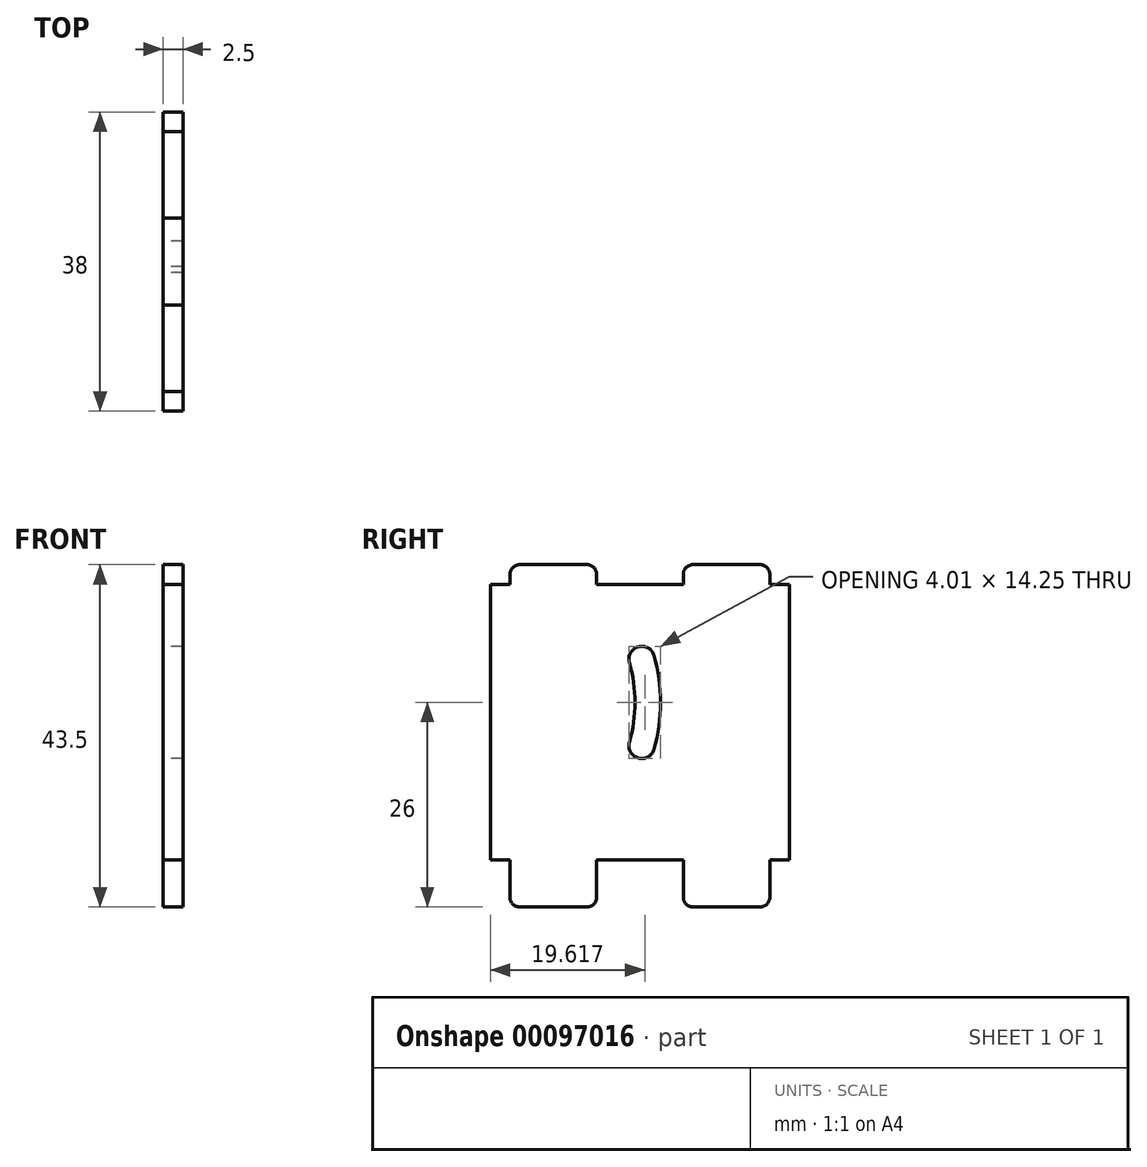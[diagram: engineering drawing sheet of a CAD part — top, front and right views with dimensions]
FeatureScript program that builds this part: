
annotation { "Feature Type Name" : "Feature", "Feature Type Description" : "" }
export const myFeature = defineFeature(function(context is Context, id is Id, definition is map)
    precondition{}
    {
        {
            var Q0;
            Q0=qCreatedBy(makeId("Right.planeOp"),FACE);
            var sketch = newSketch(context, id + "F0", { "sketchPlane" : qUnion([Q0])});
            skLineSegment(sketch, "E0.bottom", {"start": v(-19, 17.5) * mm, "end": v(-16.5, 17.5) * mm});
            skLineSegment(sketch, "E0.top", {"start": v(-19, -17.5) * mm, "end": v(-16.5, -17.5) * mm});
            skLineSegment(sketch, "E0.left", {"start": v(-19, 17.5) * mm, "end": v(-19, -17.5) * mm});
            skLineSegment(sketch, "E0.right", {"start": v(19, 17.5) * mm, "end": v(19, -17.5) * mm});
            skPoint(sketch, "E0.middle", {"position": v(0, 0) * mm});
            skPoint(sketch, "E1", {"position": v(-19, 2.5) * mm});
            skLineSegment(sketch, "E2", {"start": v(-19, 2.5) * mm, "end": v(-0.63, 2.82) * mm});
            skLineSegment(sketch, "E3", {"start": v(-19, 2.5) * mm, "end": v(-1.34, -2.56) * mm});
            skLineSegment(sketch, "E4", {"start": v(-19, 2.5) * mm, "end": v(-1.34, 7.56) * mm});
            skArc(sketch, "E5", {"start": v(1.79, 8.46) * mm, "mid": v(-0.22, 9.57) * mm, "end": v(-1.34, 7.56) * mm});
            skArc(sketch, "E6", {"start": v(-1.34, -2.56) * mm, "mid": v(-0.22, -4.57) * mm, "end": v(1.79, -3.46) * mm});
            skPoint(sketch, "E7", {"position": v(-0.63, 2.82) * mm});
            skPoint(sketch, "E8", {"position": v(-1.34, 7.56) * mm});
            skPoint(sketch, "E9", {"position": v(-1.34, -2.56) * mm});
            skArc(sketch, "E10", {"start": v(1.79, -3.46) * mm, "mid": v(2.62, 2.5) * mm, "end": v(1.79, 8.46) * mm});
            skArc(sketch, "E11", {"start": v(-1.34, -2.56) * mm, "mid": v(-0.63, 2.5) * mm, "end": v(-1.34, 7.56) * mm});
            skPoint(sketch, "E12.end.orphan", {"position": v(2.62, 2.82) * mm});
            skLineSegment(sketch, "E13.bottom", {"start": v(-5.5, 17.5) * mm, "end": v(5.5, 17.5) * mm});
            skLineSegment(sketch, "E13.top", {"start": v(-15.25, 20) * mm, "end": v(-6.75, 20) * mm});
            skLineSegment(sketch, "E13.left", {"start": v(-16.5, 17.5) * mm, "end": v(-16.5, 18.75) * mm});
            skLineSegment(sketch, "E13.right", {"start": v(16.5, 17.5) * mm, "end": v(16.5, 18.75) * mm});
            skLineSegment(sketch, "E14.bottom", {"start": v(-5.5, -17.5) * mm, "end": v(5.5, -17.5) * mm});
            skLineSegment(sketch, "E14.top", {"start": v(-15.25, -23.5) * mm, "end": v(-6.75, -23.5) * mm});
            skLineSegment(sketch, "E14.left", {"start": v(-16.5, -17.5) * mm, "end": v(-16.5, -22.25) * mm});
            skLineSegment(sketch, "E14.right", {"start": v(16.5, -17.5) * mm, "end": v(16.5, -22.25) * mm});
            skLineSegment(sketch, "E15", {"start": v(5.5, 18.75) * mm, "end": v(5.5, 17.5) * mm});
            skLineSegment(sketch, "E16", {"start": v(-5.5, 18.75) * mm, "end": v(-5.5, 17.5) * mm});
            skLineSegment(sketch, "E17", {"start": v(5.5, -17.5) * mm, "end": v(5.5, -22.25) * mm});
            skLineSegment(sketch, "E18", {"start": v(-5.5, -17.5) * mm, "end": v(-5.5, -22.25) * mm});
            skLineSegment(sketch, "E19.trimOffspring", {"start": v(6.75, 20) * mm, "end": v(15.25, 20) * mm});
            skLineSegment(sketch, "E20.trimOffspring", {"start": v(6.75, -23.5) * mm, "end": v(15.25, -23.5) * mm});
            skLineSegment(sketch, "E21.trimOffspring", {"start": v(16.5, 17.5) * mm, "end": v(19, 17.5) * mm});
            skLineSegment(sketch, "E22.trimOffspring", {"start": v(16.5, -17.5) * mm, "end": v(19, -17.5) * mm});
            skPoint(sketch, "E23", {"position": v(-16.5, 18.75) * mm});
            skPoint(sketch, "E24", {"position": v(-5.5, 18.75) * mm});
            skPoint(sketch, "E25", {"position": v(5.5, 18.75) * mm});
            skPoint(sketch, "E26", {"position": v(16.5, 18.75) * mm});
            skPoint(sketch, "E27", {"position": v(16.5, -22.25) * mm});
            skPoint(sketch, "E28", {"position": v(5.5, -22.25) * mm});
            skPoint(sketch, "E29", {"position": v(-5.5, -22.25) * mm});
            skPoint(sketch, "E30", {"position": v(-16.5, -22.25) * mm});
            skPoint(sketch, "E31", {"position": v(15.25, -23.5) * mm});
            skPoint(sketch, "E32", {"position": v(6.75, -23.5) * mm});
            skPoint(sketch, "E33", {"position": v(-6.75, -23.5) * mm});
            skPoint(sketch, "E34", {"position": v(-15.25, -23.5) * mm});
            skPoint(sketch, "E35", {"position": v(-15.25, 20) * mm});
            skPoint(sketch, "E36", {"position": v(-6.75, 20) * mm});
            skPoint(sketch, "E37", {"position": v(6.75, 20) * mm});
            skPoint(sketch, "E38", {"position": v(15.25, 20) * mm});
            skArc(sketch, "E39", {"start": v(-15.25, 20) * mm, "mid": v(-16.13, 19.63) * mm, "end": v(-16.5, 18.75) * mm});
            skArc(sketch, "E40", {"start": v(-5.5, 18.75) * mm, "mid": v(-5.87, 19.63) * mm, "end": v(-6.75, 20) * mm});
            skArc(sketch, "E41", {"start": v(6.75, 20) * mm, "mid": v(5.87, 19.63) * mm, "end": v(5.5, 18.75) * mm});
            skArc(sketch, "E42", {"start": v(16.5, 18.75) * mm, "mid": v(16.13, 19.63) * mm, "end": v(15.25, 20) * mm});
            skArc(sketch, "E43", {"start": v(15.25, -23.5) * mm, "mid": v(16.13, -23.13) * mm, "end": v(16.5, -22.25) * mm});
            skArc(sketch, "E44", {"start": v(5.5, -22.25) * mm, "mid": v(5.87, -23.13) * mm, "end": v(6.75, -23.5) * mm});
            skArc(sketch, "E45", {"start": v(-6.75, -23.5) * mm, "mid": v(-5.87, -23.13) * mm, "end": v(-5.5, -22.25) * mm});
            skArc(sketch, "E46", {"start": v(-16.5, -22.25) * mm, "mid": v(-16.13, -23.13) * mm, "end": v(-15.25, -23.5) * mm});
            skLineSegment(sketch, "E47", {"start": v(16.5, 17.5) * mm, "end": v(5.5, 17.5) * mm});
            skLineSegment(sketch, "E48", {"start": v(-5.5, 17.5) * mm, "end": v(-16.5, 17.5) * mm});
            skLineSegment(sketch, "E49", {"start": v(16.5, -17.5) * mm, "end": v(5.5, -17.5) * mm});
            skLineSegment(sketch, "E50", {"start": v(-5.5, -17.5) * mm, "end": v(-16.5, -17.5) * mm});
            skLineSegment(sketch, "E51", {"start": v(-0.63, 2.82) * mm, "end": v(2.62, 2.82) * mm});
            skPoint(sketch, "E52", {"position": v(1, 2.82) * mm});
            skLineSegment(sketch, "E53", {"start": v(-1.34, 7.56) * mm, "end": v(1.79, 8.46) * mm});
            skLineSegment(sketch, "E54", {"start": v(-1.34, -2.56) * mm, "end": v(1.79, -3.46) * mm});
            skSolve(sketch);
        }
        {
            var Q0;
            {var subQ1=sQuery(id+"F0.wireOp",EDGE,"E0.bottom");Q0=makeQuery(id+"F0.imprint","IMPRINT",FACE,{"disambiguationData":[TD([[makeQuery(id+"F0.imprint","IMPRINT",EDGE,{"derivedFrom":subQ1}),-1.0]])]});}
            var Q1;
            {var subQ0=sQuery(id+"F0.wireOp",EDGE,"E2");Q1=makeQuery(id+"F0.imprint","IMPRINT",FACE,{"disambiguationData":[TD([[makeQuery(id+"F0.imprint","IMPRINT",EDGE,{"derivedFrom":subQ0}),1.0]])]});}
            var Q2;
            {var subQ0=sQuery(id+"F0.wireOp",EDGE,"E2");Q2=makeQuery(id+"F0.imprint","IMPRINT",FACE,{"disambiguationData":[TD([[makeQuery(id+"F0.imprint","IMPRINT",EDGE,{"derivedFrom":subQ0}),-1.0]])]});}
            var Q3;
            Q3=makeQuery(id+"F0.imprint","IMPRINT",FACE,{"disambiguationData":[TD([[makeQuery(id+"F0.imprint","IMPRINT",EDGE,{"derivedFrom":sQuery(id+"F0.wireOp",EDGE,"E14.top")}),1.0]])]});
            var Q4;
            Q4=makeQuery(id+"F0.imprint","IMPRINT",FACE,{"disambiguationData":[TD([[makeQuery(id+"F0.imprint","IMPRINT",EDGE,{"derivedFrom":sQuery(id+"F0.wireOp",EDGE,"E14.right")}),-1.0]])]});
            var Q5;
            Q5=makeQuery(id+"F0.imprint","IMPRINT",FACE,{"disambiguationData":[TD([[makeQuery(id+"F0.imprint","IMPRINT",EDGE,{"derivedFrom":sQuery(id+"F0.wireOp",EDGE,"E13.right")}),1.0]])]});
            var Q6;
            Q6=makeQuery(id+"F0.imprint","IMPRINT",FACE,{"disambiguationData":[TD([[makeQuery(id+"F0.imprint","IMPRINT",EDGE,{"derivedFrom":sQuery(id+"F0.wireOp",EDGE,"E13.top")}),-1.0]])]});
            extrude(context, id + "F1", {"entities" : qUnion([Q0, Q1, Q2, Q3, Q4, Q5, Q6]), "depth" : 2.5 * mm});
        }
    });
